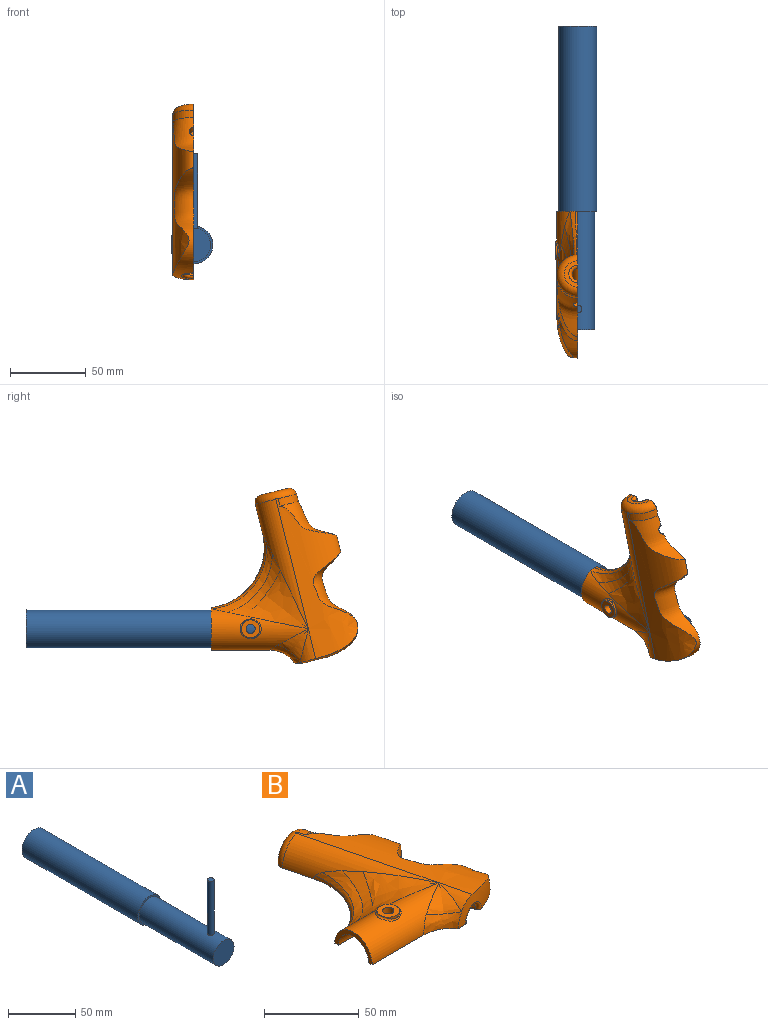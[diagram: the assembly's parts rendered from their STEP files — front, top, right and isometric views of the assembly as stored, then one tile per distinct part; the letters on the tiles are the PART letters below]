
ASSEMBLY  parts=2 mates=1
PART A: 7 faces, bbox 25x200x72.5 mm
  f0: cylinder r=11mm len=78mm, axis (0,-1,0), area 5371.3mm2, adj f3,f4,f5
  f1: cylinder r=12.5mm len=122mm, axis (0,1,0), area 9581.9mm2, adj f2,f3
  f2: plane 25x25mm, normal (0,1,0), area 490.9mm2, adj f1
  f3: plane 25x25mm, normal (0,-1,0), area 110.7mm2, adj f0,f1
  f4: plane 22x22mm, normal (0,-1,0), area 380.1mm2, adj f0
  f5: cylinder r=2.5mm len=49.29mm, axis (0,0,-1), area 771.9mm2, adj f0,f6
  f6: plane 5x5mm, normal (0,0,1), area 19.6mm2, adj f5
PART B: 35 faces, bbox 102.5x118.1x36.2 mm
  f0: cylinder r=4mm len=78.49mm, axis (-0.24,0.97,0), area 957.3mm2, adj f1,f30,f31,f32,f33,f34
  f1: torus R=6mm, axis (-0.24,0.97,0), area 46.7mm2, adj f0,f2,f30,f34
  f2: plane 17.47x9mm, normal (-0.24,0.97,0), area 70.7mm2, adj f1,f3,f30,f34
  f3: torus R=9mm, axis (-0.24,0.97,0), area 300.2mm2, adj f2,f4,f6,f29,f30,f34
  f4: cylinder r=14mm len=13.93mm, axis (0.24,-0.97,0), area 103mm2, adj f3,f5,f6,f30
  f5: revolved ~37.42x32.84mm, area 445.1mm2, adj f4,f6,f30,f31,f32
  f6: extruded ~113.02x58.21mm, area 2214.2mm2, adj f3,f4,f5,f7,f28,f29,f32
  f7: revolved ~75.4x73.79mm, area 1098.2mm2, adj f6,f8,f26,f27,f28,f32
  f8: torus R=8mm, axis (-0.24,0.97,0), area 72.7mm2, adj f7,f9,f26,f32
  f9: cylinder r=6mm len=13.71mm, axis (0.24,-0.97,0), area 127.7mm2, adj f8,f10,f26,f32
  f10: bspline ~16.51x7.64mm, area 53.3mm2, adj f9,f11,f26,f32
  f11: cylinder r=11.25mm len=78mm, axis (-1,0,0), area 2584.7mm2, adj f10,f12,f24,f25,f26,f32,f33,f34
  f12: cylinder r=3mm len=6mm, axis (0,0,1), area 70.7mm2, adj f11,f13
  f13: plane 12x12mm, normal (0,0,1), area 84.8mm2, adj f12,f14,f23
  f14: cylinder r=6mm len=12mm, axis (0,0,1), area 16.1mm2, adj f13,f15
  f15: bspline ~14.02x13.08mm, area 53.2mm2, adj f14,f16,f23
  f16: cylinder r=14mm len=64mm, axis (-1,0,0), area 1379.6mm2, adj f15,f17,f20,f21,f22,f24,f26,f27
  f17: bspline ~48.17x40.64mm, area 334.6mm2, adj f16,f18,f20,f29
  f18: bspline ~49.81x36.47mm, area 186.1mm2, adj f17,f19,f24,f29
  f19: bspline ~49.47x35.04mm, area 89.4mm2, adj f18,f24,f29,f34
  f20: bspline ~40.7x35.05mm, area 306.8mm2, adj f16,f17,f21,f29
  f21: bspline ~47.26x43.54mm, area 468mm2, adj f16,f20,f29
  f22: bspline ~22.16x20.19mm, area 128mm2, adj f16,f27,f28
  f23: cylinder r=6mm len=12mm, axis (0,0,1), area 0mm2, adj f13,f15
  f24: plane 28.01x14.01mm, normal (-1,0,0), area 109.1mm2, adj f11,f16,f18,f19,f26,f34
  f25: plane 22.5x11.25mm, normal (-1,0,0), area 198.8mm2, adj f11,f32
  f26: plane 63.01x11.89mm, normal (0,0,-1), area 271.4mm2, adj f7,f8,f9,f10,f11,f16,f24,f27
  f27: bspline ~20.88x13.27mm, area 177.2mm2, adj f7,f16,f22,f26
  f28: cylinder r=14mm len=22.16mm, axis (0.24,-0.97,0), area 122mm2, adj f6,f7,f22
  f29: cylinder r=14mm len=88.83mm, axis (0.24,-0.97,0), area 973.9mm2, adj f3,f6,f17,f18,f19,f20,f21,f34
  f30: plane 17.85x14.91mm, normal (0,0,-1), area 168.8mm2, adj f0,f1,f2,f3,f4,f5,f31
  f31: cylinder r=3mm len=13.59mm, axis (-0.97,-0.24,0), area 112.9mm2, adj f0,f5,f30,f32
  f32: plane 91.22x46.32mm, normal (0,0,-1), area 1635.3mm2, adj f0,f5,f6,f7,f8,f9,f10,f11
  f33: bspline ~12.38x6.05mm, area 39.4mm2, adj f0,f11,f32,f34
  f34: plane 79.25x58.11mm, normal (0,0,-1), area 1492.7mm2, adj f0,f1,f2,f3,f11,f19,f24,f29
PLACE A t=(-54.88,21.15,-64.94)mm
PLACE B rot(axis=(0.58,-0.58,-0.58),120deg) t=(-54.88,-100.85,-64.94)mm
MATE fastened A.f0 <-> B.f11  axis (0,-1,0) through (-54.88,-139.85,-64.94)mm
